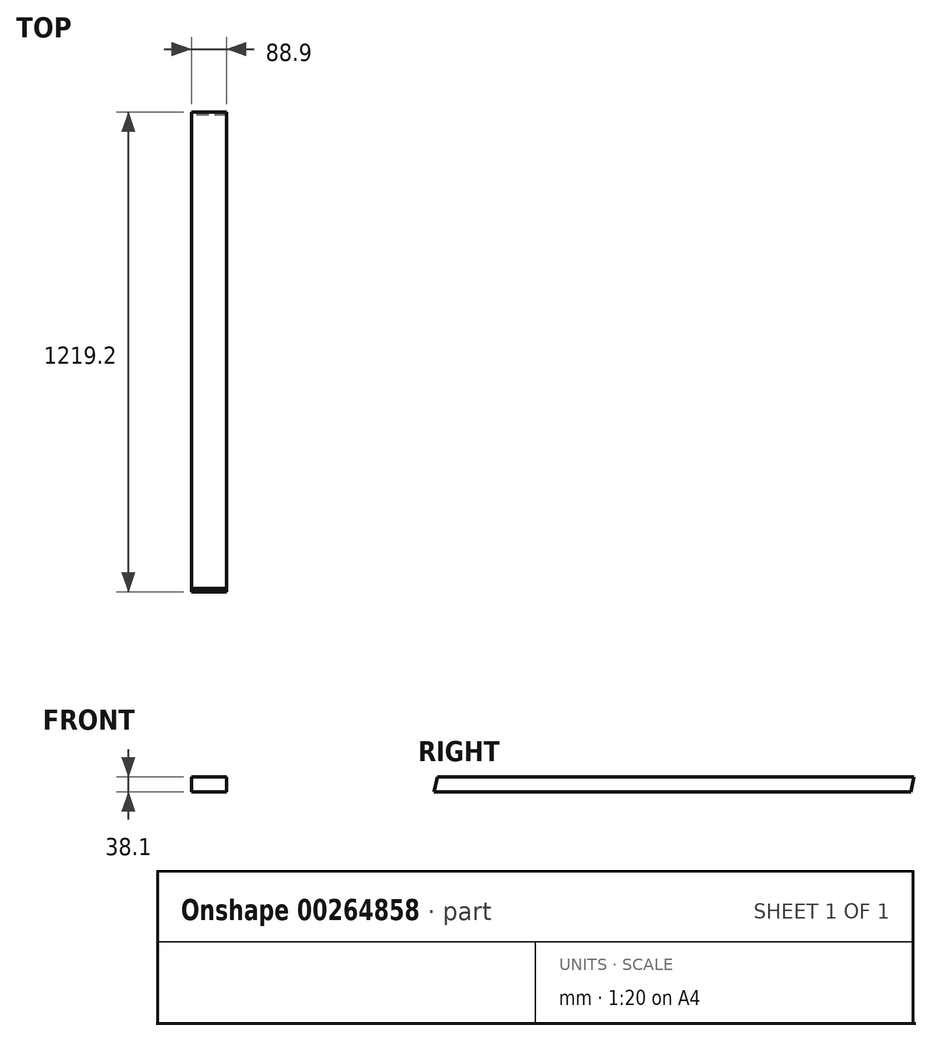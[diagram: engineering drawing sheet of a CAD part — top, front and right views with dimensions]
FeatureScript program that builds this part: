
annotation { "Feature Type Name" : "Feature", "Feature Type Description" : "" }
export const myFeature = defineFeature(function(context is Context, id is Id, definition is map)
    precondition{}
    {
        {
            var Q0;
            Q0=qCreatedBy(makeId("Top.planeOp"),FACE);
            var sketch = newSketch(context, id + "F0", { "sketchPlane" : qUnion([Q0])});
            skLineSegment(sketch, "E0.bottom", {"start": v(0, 0) * mm, "end": v(88.9, 0) * mm});
            skLineSegment(sketch, "E0.top", {"start": v(0, 1219.2) * mm, "end": v(88.9, 1219.2) * mm});
            skLineSegment(sketch, "E0.left", {"start": v(0, 0) * mm, "end": v(0, 1219.2) * mm});
            skLineSegment(sketch, "E0.right", {"start": v(88.9, 0) * mm, "end": v(88.9, 1219.2) * mm});
            skSolve(sketch);
        }
        {
            var Q0;
            Q0=makeQuery(id+"F0.imprint","IMPRINT",FACE,{"disambiguationData":[TD([[makeQuery(id+"F0.imprint","IMPRINT",EDGE,{"derivedFrom":sQuery(id+"F0.wireOp",EDGE,"E0.bottom")}),1.0]])]});
            extrude(context, id + "F1", {"entities" : qUnion([Q0]), "depth" : 38.1 * mm, "offsetDistance" : 25.4 * mm});
        }
        {
            var Q0;
            Q0=makeQuery(id+"F1.opExtrude","SWEPT_FACE",FACE,{"disambiguationData":[OSD([sQuery(id+"F0.wireOp",EDGE,"E0.left")])]});
            var sketch = newSketch(context, id + "F2", { "sketchPlane" : qUnion([Q0])});
            skLineSegment(sketch, "E1", {"start": v(-1219.2, -37.16) * mm, "end": v(-1219.2, 38.1) * mm});
            skLineSegment(sketch, "E2", {"start": v(-1219.2, 38.1) * mm, "end": v(-1203.01, -37.16) * mm});
            skLineSegment(sketch, "E3", {"start": v(-1203.01, -37.16) * mm, "end": v(-1219.2, -37.16) * mm});
            skLineSegment(sketch, "E4", {"start": v(0, 69.17) * mm, "end": v(0, 0) * mm});
            skLineSegment(sketch, "E5", {"start": v(0, 0) * mm, "end": v(-14.88, 69.17) * mm});
            skLineSegment(sketch, "E6", {"start": v(-14.88, 69.17) * mm, "end": v(0, 69.17) * mm});
            skSolve(sketch);
        }
        {
            var Q0;
            {var subQ1=sQuery(id+"F2.wireOp",EDGE,"E4");var subQ2=sQuery(id+"F0.wireOp",EDGE,"E0.left");var subQ4=makeQuery(id+"F1.opExtrude","CAP_EDGE",EDGE,{"disambiguationData":[OSD([subQ2])],"isStart":false});var subQ5=makeQuery(id+"F2.imprint","INTERSECT",VERTEX,{"derivedFrom":[subQ4,subQ1]});Q0=makeQuery(id+"F2.imprint","IMPRINT",FACE,{"disambiguationData":[TD([[makeQuery(id+"F2.imprint","IMPRINT",EDGE,{"disambiguationData":[TD([[subQ5,-1.0]])],"derivedFrom":subQ4}),1.0]])]});}
            var Q1;
            {var subQ0=sQuery(id+"F2.wireOp",EDGE,"E1");var subQ1=sQuery(id+"F0.wireOp",EDGE,"E0.left");var subQ2=makeQuery(id+"F1.opExtrude","CAP_EDGE",EDGE,{"disambiguationData":[OSD([subQ1])],"isStart":true});var subQ3=makeQuery(id+"F2.imprint","INTERSECT",VERTEX,{"derivedFrom":[subQ2,subQ0]});Q1=makeQuery(id+"F2.imprint","IMPRINT",FACE,{"disambiguationData":[TD([[makeQuery(id+"F2.imprint","IMPRINT",EDGE,{"disambiguationData":[TD([[subQ3,1.0]])],"derivedFrom":subQ2}),-1.0]])]});}
            extrude(context, id + "F3", {"entities" : qUnion([Q0, Q1]), "operationType" : NewBodyOperationType.REMOVE, "endBound" : BoundingType.THROUGH_ALL, "oppositeDirection" : true, "depth" : 25.4 * mm, "offsetDistance" : 25.4 * mm});
        }
    });
